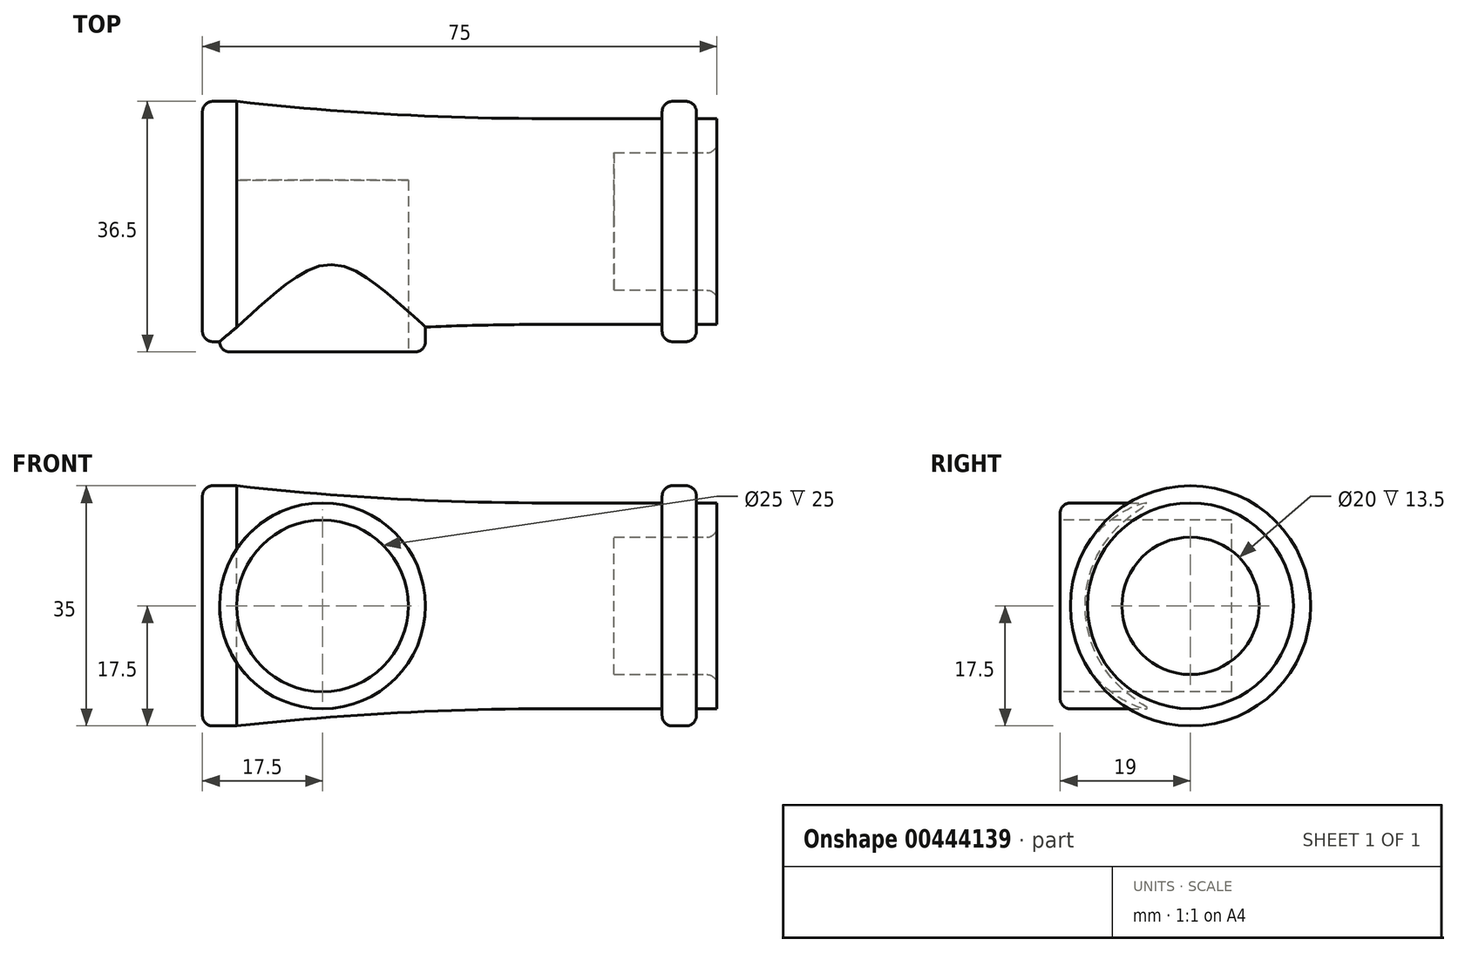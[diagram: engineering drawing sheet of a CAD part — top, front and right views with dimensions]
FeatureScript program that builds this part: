
annotation { "Feature Type Name" : "Feature", "Feature Type Description" : "" }
export const myFeature = defineFeature(function(context is Context, id is Id, definition is map)
    precondition{}
    {
        {
            var Q0;
            Q0=qCreatedBy(makeId("Front.planeOp"),FACE);
            var sketch = newSketch(context, id + "F0", { "sketchPlane" : qUnion([Q0])});
            skLineSegment(sketch, "E0", {"start": v(0, 0) * mm, "end": v(0, 17.5) * mm});
            skLineSegment(sketch, "E1", {"start": v(0, 17.5) * mm, "end": v(5, 17.5) * mm});
            skArc(sketch, "E2", {"start": v(5, 17.5) * mm, "mid": v(27.47, 15.63) * mm, "end": v(50, 15) * mm});
            skLineSegment(sketch, "E3", {"start": v(50, 15) * mm, "end": v(67, 15) * mm});
            skLineSegment(sketch, "E4", {"start": v(67, 15) * mm, "end": v(67, 17.5) * mm});
            skLineSegment(sketch, "E5", {"start": v(67, 17.5) * mm, "end": v(72, 17.5) * mm});
            skLineSegment(sketch, "E6", {"start": v(72, 17.5) * mm, "end": v(72, 15) * mm});
            skLineSegment(sketch, "E7", {"start": v(72, 15) * mm, "end": v(75, 15) * mm});
            skLineSegment(sketch, "E8", {"start": v(75, 15) * mm, "end": v(75, 10) * mm});
            skLineSegment(sketch, "E9", {"start": v(75, 10) * mm, "end": v(60, 10) * mm});
            skLineSegment(sketch, "E10", {"start": v(60, 10) * mm, "end": v(60, 0) * mm});
            skLineSegment(sketch, "E11", {"start": v(60, 0) * mm, "end": v(0, 0) * mm});
            skSolve(sketch);
        }
        {
            var Q0;
            Q0 = qSketchRegion(id + "F0", true);
            var Q1;
            Q1=sQuery(id+"F0.wireOp",EDGE,"E11");
            revolve(context, id + "F1", {"entities" : qUnion([Q0]), "axis" : qUnion([Q1]), "revolveType" : RevolveType.FULL});
        }
        {
            var Q0;
            Q0=qCreatedBy(makeId("Front.planeOp"),FACE);
            var sketch = newSketch(context, id + "F2", { "sketchPlane" : qUnion([Q0])});
            skCircle(sketch, "E12", {"center": v(17.5, 0) * mm, "radius": 15 * mm});
            skSolve(sketch);
        }
        {
            var Q0;
            Q0 = qSketchRegion(id + "F2", true);
            extrude(context, id + "F3", {"entities" : qUnion([Q0]), "operationType" : NewBodyOperationType.ADD, "depth" : 19 * mm});
        }
        {
            var Q0;
            Q0=makeQuery(id+"F3.opExtrude","CAP_FACE",FACE,{"disambiguationData":[OSD([sQuery(id+"F2.wireOp",EDGE,"E12")])],"isStart":false});
            var sketch = newSketch(context, id + "F4", { "sketchPlane" : qUnion([Q0])});
            skCircle(sketch, "E13", {"center": v(17.5, 0) * mm, "radius": 12.5 * mm});
            skSolve(sketch);
        }
        {
            var Q0;
            Q0 = qSketchRegion(id + "F4", true);
            extrude(context, id + "F5", {"entities" : qUnion([Q0]), "operationType" : NewBodyOperationType.REMOVE, "oppositeDirection" : true, "depth" : 25 * mm});
        }
        {
            var Q0;
            Q0=makeQuery(id+"F3.opExtrude","CAP_EDGE",EDGE,{"disambiguationData":[OSD([sQuery(id+"F2.wireOp",EDGE,"E12")])],"isStart":false});
            var Q1;
            Q1=makeQuery(id+"F1.opRevolve","SWEPT_EDGE",EDGE,{"disambiguationData":[OSD([sQuery(id+"F0.wireOp",EDGE,"E5"),sQuery(id+"F0.wireOp",EDGE,"E6")])]});
            var Q2;
            Q2=makeQuery(id+"F1.opRevolve","SWEPT_EDGE",EDGE,{"disambiguationData":[OSD([sQuery(id+"F0.wireOp",EDGE,"E8"),sQuery(id+"F0.wireOp",EDGE,"E9")])]});
            var Q3;
            Q3=makeQuery(id+"F1.opRevolve","SWEPT_EDGE",EDGE,{"disambiguationData":[OSD([sQuery(id+"F0.wireOp",EDGE,"E4"),sQuery(id+"F0.wireOp",EDGE,"E5")])]});
            var Q4;
            Q4=makeQuery(id+"F1.opRevolve","SWEPT_EDGE",EDGE,{"disambiguationData":[OSD([sQuery(id+"F0.wireOp",EDGE,"E0"),sQuery(id+"F0.wireOp",EDGE,"E1")])]});
            fillet(context, id + "F6", {"entities" : qUnion([Q0, Q1, Q2, Q3, Q4]), "radius" : 1.5 * mm, "tangentPropagation" : true, "allowEdgeOverflow" : false});
        }
    });
